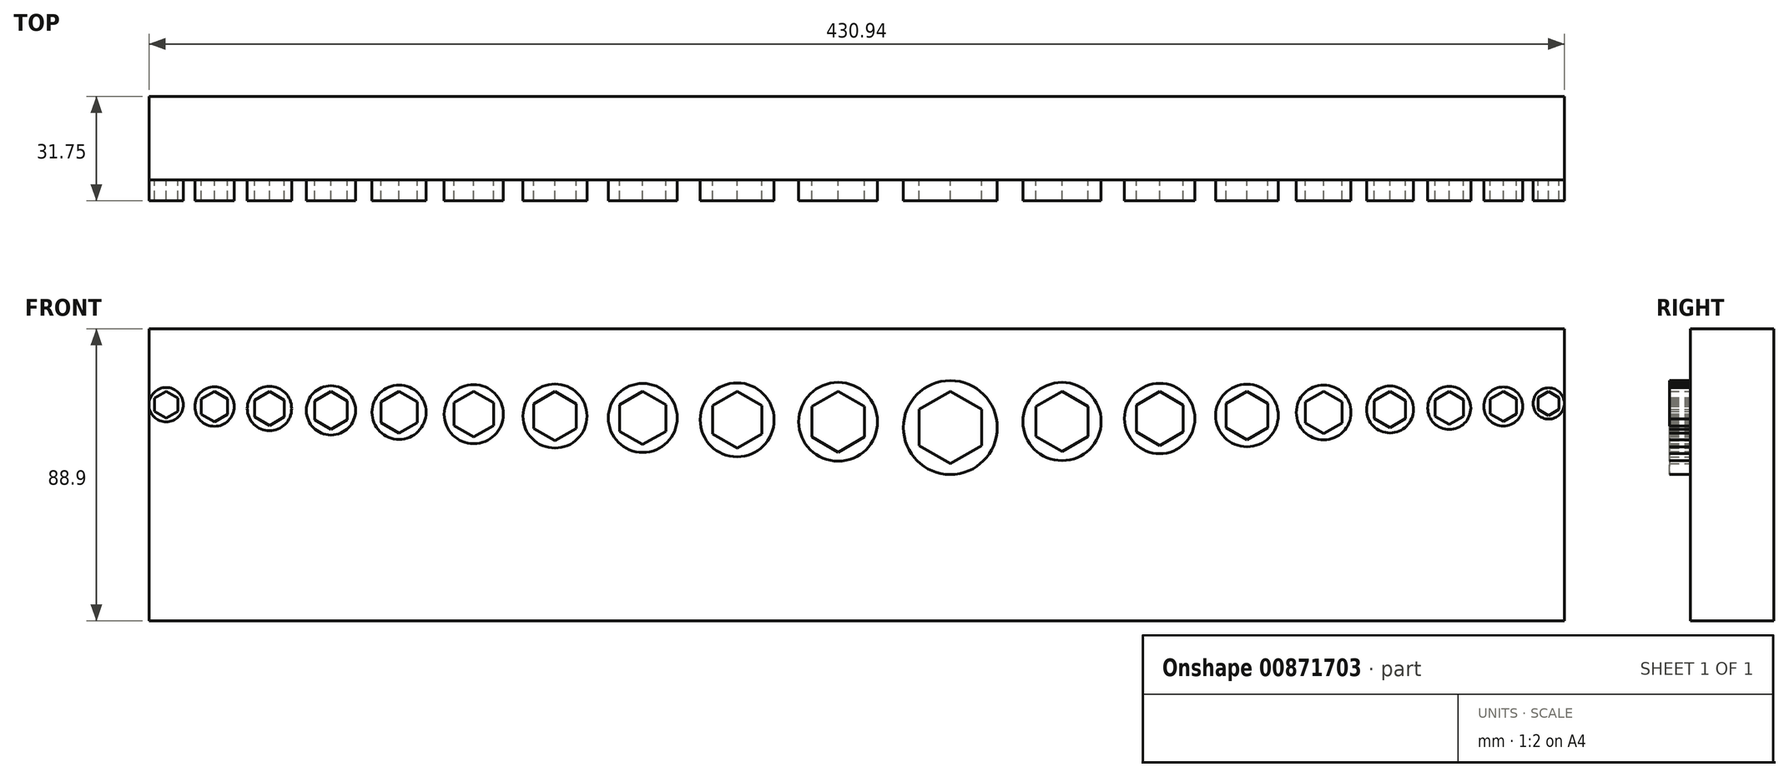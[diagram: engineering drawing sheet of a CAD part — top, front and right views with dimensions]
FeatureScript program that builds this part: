
annotation { "Feature Type Name" : "Feature", "Feature Type Description" : "" }
export const myFeature = defineFeature(function(context is Context, id is Id, definition is map)
    precondition{}
    {
        {
            var Q0;
            Q0=qCreatedBy(makeId("Front.planeOp"),FACE);
            var sketch = newSketch(context, id + "F0", { "sketchPlane" : qUnion([Q0])});
            skPoint(sketch, "E0.middle", {"position": v(0, 0) * mm});
            skLineSegment(sketch, "E1", {"start": v(-190.5, 0) * mm, "end": v(190.5, 0) * mm, "construction": true});
            skSolve(sketch);
        }
        {
            var Q0;
            Q0=qCreatedBy(makeId("Front.planeOp"),FACE);
            var sketch = newSketch(context, id + "F1", { "sketchPlane" : qUnion([Q0])});
            skCircle(sketch, "E2.cCircle", {"center": v(17, -9.24) * mm, "radius": 8 * mm, "construction": true});
            skLineSegment(sketch, "E2.0", {"start": v(25, -4.62) * mm, "end": v(25, -13.86) * mm});
            skLineSegment(sketch, "E2.1", {"start": v(25, -13.86) * mm, "end": v(17, -18.48) * mm});
            skLineSegment(sketch, "E2.2", {"start": v(17, -18.48) * mm, "end": v(9, -13.86) * mm});
            skLineSegment(sketch, "E2.3", {"start": v(9, -13.86) * mm, "end": v(9, -4.62) * mm});
            skLineSegment(sketch, "E2.4", {"start": v(9, -4.62) * mm, "end": v(17, 0) * mm});
            skLineSegment(sketch, "E2.5", {"start": v(17, 0) * mm, "end": v(25, -4.62) * mm});
            skPoint(sketch, "E2.0.midPoint", {"position": v(25, -9.24) * mm});
            skCircle(sketch, "E3", {"center": v(17, -9.24) * mm, "radius": 12 * mm});
            skLineSegment(sketch, "E4", {"start": v(17, -9.24) * mm, "end": v(9, -9.24) * mm, "construction": true});
            skLineSegment(sketch, "E5", {"start": v(13, -9.24) * mm, "end": v(17, -9.24) * mm, "construction": true});
            skLineSegment(sketch, "E6", {"start": v(25, -9.24) * mm, "end": v(29, -9.24) * mm, "construction": true});
            skCircle(sketch, "E7.cCircle", {"center": v(-13.74, -8.66) * mm, "radius": 7.5 * mm, "construction": true});
            skLineSegment(sketch, "E7.0", {"start": v(-6.24, -4.33) * mm, "end": v(-6.24, -13) * mm});
            skLineSegment(sketch, "E7.1", {"start": v(-6.24, -13) * mm, "end": v(-13.74, -17.32) * mm});
            skLineSegment(sketch, "E7.2", {"start": v(-13.74, -17.32) * mm, "end": v(-21.24, -13) * mm});
            skLineSegment(sketch, "E7.3", {"start": v(-21.24, -13) * mm, "end": v(-21.24, -4.33) * mm});
            skLineSegment(sketch, "E7.4", {"start": v(-21.24, -4.33) * mm, "end": v(-13.74, 0) * mm});
            skLineSegment(sketch, "E7.5", {"start": v(-13.74, 0) * mm, "end": v(-6.24, -4.33) * mm});
            skPoint(sketch, "E7.0.midPoint", {"position": v(-6.24, -8.66) * mm});
            skCircle(sketch, "E8", {"center": v(-13.74, -8.66) * mm, "radius": 11.25 * mm});
            skLineSegment(sketch, "E9", {"start": v(-13.74, -8.66) * mm, "end": v(-21.24, -8.66) * mm, "construction": true});
            skLineSegment(sketch, "E10", {"start": v(-17.5, -8.66) * mm, "end": v(-13.74, -8.66) * mm, "construction": true});
            skLineSegment(sketch, "E11", {"start": v(-6.24, -8.66) * mm, "end": v(-2.5, -8.66) * mm, "construction": true});
            skLineSegment(sketch, "E12", {"start": v(-13.74, 0) * mm, "end": v(-13.74, -17.32) * mm, "construction": true});
            skLineSegment(sketch, "E13", {"start": v(17, 0) * mm, "end": v(17, -18.48) * mm, "construction": true});
            skLineSegment(sketch, "E14", {"start": v(-2.5, -8.66) * mm, "end": v(5, -8.66) * mm, "construction": true});
            skCircle(sketch, "E15.cCircle", {"center": v(-42.48, -8.08) * mm, "radius": 7 * mm, "construction": true});
            skLineSegment(sketch, "E15.0", {"start": v(-35.48, -4.04) * mm, "end": v(-35.48, -12.12) * mm});
            skLineSegment(sketch, "E15.1", {"start": v(-35.48, -12.12) * mm, "end": v(-42.48, -16.17) * mm});
            skLineSegment(sketch, "E15.2", {"start": v(-42.48, -16.17) * mm, "end": v(-49.48, -12.12) * mm});
            skLineSegment(sketch, "E15.3", {"start": v(-49.48, -12.12) * mm, "end": v(-49.48, -4.04) * mm});
            skLineSegment(sketch, "E15.4", {"start": v(-49.48, -4.04) * mm, "end": v(-42.48, 0) * mm});
            skLineSegment(sketch, "E15.5", {"start": v(-42.48, 0) * mm, "end": v(-35.48, -4.04) * mm});
            skPoint(sketch, "E15.0.midPoint", {"position": v(-35.48, -8.08) * mm});
            skCircle(sketch, "E16", {"center": v(-42.48, -8.08) * mm, "radius": 10.5 * mm});
            skLineSegment(sketch, "E17", {"start": v(-42.48, -8.08) * mm, "end": v(-49.48, -8.08) * mm, "construction": true});
            skLineSegment(sketch, "E18", {"start": v(-45.98, -8.08) * mm, "end": v(-42.48, -8.08) * mm, "construction": true});
            skLineSegment(sketch, "E19", {"start": v(-35.48, -8.08) * mm, "end": v(-31.98, -8.08) * mm, "construction": true});
            skLineSegment(sketch, "E20", {"start": v(-42.48, 0) * mm, "end": v(-42.48, -16.17) * mm, "construction": true});
            skLineSegment(sketch, "E21", {"start": v(-31.98, -8.08) * mm, "end": v(-24.98, -8.08) * mm, "construction": true});
            skCircle(sketch, "E22.cCircle", {"center": v(-69.21, -7.5) * mm, "radius": 6.5 * mm, "construction": true});
            skLineSegment(sketch, "E22.0", {"start": v(-62.71, -3.75) * mm, "end": v(-62.71, -11.26) * mm});
            skLineSegment(sketch, "E22.1", {"start": v(-62.71, -11.26) * mm, "end": v(-69.21, -15.01) * mm});
            skLineSegment(sketch, "E22.2", {"start": v(-69.21, -15.01) * mm, "end": v(-75.71, -11.26) * mm});
            skLineSegment(sketch, "E22.3", {"start": v(-75.71, -11.26) * mm, "end": v(-75.71, -3.75) * mm});
            skLineSegment(sketch, "E22.4", {"start": v(-75.71, -3.75) * mm, "end": v(-69.21, 0) * mm});
            skLineSegment(sketch, "E22.5", {"start": v(-69.21, 0) * mm, "end": v(-62.71, -3.75) * mm});
            skPoint(sketch, "E22.0.midPoint", {"position": v(-62.71, -7.5) * mm});
            skCircle(sketch, "E23", {"center": v(-69.21, -7.5) * mm, "radius": 9.75 * mm});
            skLineSegment(sketch, "E24", {"start": v(-69.21, -7.5) * mm, "end": v(-75.71, -7.5) * mm, "construction": true});
            skLineSegment(sketch, "E25", {"start": v(-72.46, -7.5) * mm, "end": v(-69.21, -7.5) * mm, "construction": true});
            skLineSegment(sketch, "E26", {"start": v(-62.71, -7.5) * mm, "end": v(-59.46, -7.5) * mm, "construction": true});
            skLineSegment(sketch, "E27", {"start": v(-69.21, 0) * mm, "end": v(-69.21, -15.01) * mm, "construction": true});
            skCircle(sketch, "E28.cCircle", {"center": v(-93.95, -6.93) * mm, "radius": 6 * mm, "construction": true});
            skLineSegment(sketch, "E28.0", {"start": v(-87.95, -3.46) * mm, "end": v(-87.95, -10.4) * mm});
            skLineSegment(sketch, "E28.1", {"start": v(-87.95, -10.4) * mm, "end": v(-93.95, -13.86) * mm});
            skLineSegment(sketch, "E28.2", {"start": v(-93.95, -13.86) * mm, "end": v(-99.95, -10.4) * mm});
            skLineSegment(sketch, "E28.3", {"start": v(-99.95, -10.4) * mm, "end": v(-99.95, -3.46) * mm});
            skLineSegment(sketch, "E28.4", {"start": v(-99.95, -3.46) * mm, "end": v(-93.95, 0) * mm});
            skLineSegment(sketch, "E28.5", {"start": v(-93.95, 0) * mm, "end": v(-87.95, -3.46) * mm});
            skPoint(sketch, "E28.0.midPoint", {"position": v(-87.95, -6.93) * mm});
            skCircle(sketch, "E29", {"center": v(-93.95, -6.93) * mm, "radius": 9 * mm});
            skLineSegment(sketch, "E30", {"start": v(-93.95, -6.93) * mm, "end": v(-99.95, -6.93) * mm, "construction": true});
            skLineSegment(sketch, "E31", {"start": v(-96.95, -6.93) * mm, "end": v(-93.95, -6.93) * mm, "construction": true});
            skLineSegment(sketch, "E32", {"start": v(-87.95, -6.93) * mm, "end": v(-84.95, -6.93) * mm, "construction": true});
            skLineSegment(sketch, "E33", {"start": v(-93.95, 0) * mm, "end": v(-93.95, -13.86) * mm, "construction": true});
            skCircle(sketch, "E34.cCircle", {"center": v(-116.68, -6.35) * mm, "radius": 5.5 * mm, "construction": true});
            skLineSegment(sketch, "E34.0", {"start": v(-111.18, -3.18) * mm, "end": v(-111.18, -9.53) * mm});
            skLineSegment(sketch, "E34.1", {"start": v(-111.18, -9.53) * mm, "end": v(-116.68, -12.7) * mm});
            skLineSegment(sketch, "E34.2", {"start": v(-116.68, -12.7) * mm, "end": v(-122.18, -9.53) * mm});
            skLineSegment(sketch, "E34.3", {"start": v(-122.18, -9.53) * mm, "end": v(-122.18, -3.18) * mm});
            skLineSegment(sketch, "E34.4", {"start": v(-122.18, -3.18) * mm, "end": v(-116.68, 0) * mm});
            skLineSegment(sketch, "E34.5", {"start": v(-116.68, 0) * mm, "end": v(-111.18, -3.18) * mm});
            skPoint(sketch, "E34.0.midPoint", {"position": v(-111.18, -6.35) * mm});
            skCircle(sketch, "E35", {"center": v(-116.68, -6.35) * mm, "radius": 8.25 * mm});
            skLineSegment(sketch, "E36", {"start": v(-116.68, -6.35) * mm, "end": v(-122.18, -6.35) * mm, "construction": true});
            skLineSegment(sketch, "E37", {"start": v(-119.43, -6.35) * mm, "end": v(-116.68, -6.35) * mm, "construction": true});
            skLineSegment(sketch, "E38", {"start": v(-111.18, -6.35) * mm, "end": v(-108.43, -6.35) * mm, "construction": true});
            skLineSegment(sketch, "E39", {"start": v(-116.68, 0) * mm, "end": v(-116.68, -12.7) * mm, "construction": true});
            skCircle(sketch, "E40.cCircle", {"center": v(-137.4, -5.77) * mm, "radius": 5 * mm, "construction": true});
            skLineSegment(sketch, "E40.0", {"start": v(-132.4, -2.89) * mm, "end": v(-132.4, -8.66) * mm});
            skLineSegment(sketch, "E40.1", {"start": v(-132.4, -8.66) * mm, "end": v(-137.4, -11.55) * mm});
            skLineSegment(sketch, "E40.2", {"start": v(-137.4, -11.55) * mm, "end": v(-142.4, -8.66) * mm});
            skLineSegment(sketch, "E40.3", {"start": v(-142.4, -8.66) * mm, "end": v(-142.4, -2.89) * mm});
            skLineSegment(sketch, "E40.4", {"start": v(-142.4, -2.89) * mm, "end": v(-137.4, 0) * mm});
            skLineSegment(sketch, "E40.5", {"start": v(-137.4, 0) * mm, "end": v(-132.4, -2.89) * mm});
            skPoint(sketch, "E40.0.midPoint", {"position": v(-132.4, -5.77) * mm});
            skCircle(sketch, "E41", {"center": v(-137.4, -5.77) * mm, "radius": 7.5 * mm});
            skLineSegment(sketch, "E42", {"start": v(-137.4, -5.77) * mm, "end": v(-142.4, -5.77) * mm, "construction": true});
            skLineSegment(sketch, "E43", {"start": v(-139.9, -5.77) * mm, "end": v(-137.4, -5.77) * mm, "construction": true});
            skLineSegment(sketch, "E44", {"start": v(-132.4, -5.77) * mm, "end": v(-129.9, -5.77) * mm, "construction": true});
            skLineSegment(sketch, "E45", {"start": v(-137.4, 0) * mm, "end": v(-137.4, -11.55) * mm, "construction": true});
            skCircle(sketch, "E46.cCircle", {"center": v(-156.13, -5.2) * mm, "radius": 4.5 * mm, "construction": true});
            skLineSegment(sketch, "E46.0", {"start": v(-151.63, -2.6) * mm, "end": v(-151.63, -7.8) * mm});
            skLineSegment(sketch, "E46.1", {"start": v(-151.63, -7.8) * mm, "end": v(-156.13, -10.4) * mm});
            skLineSegment(sketch, "E46.2", {"start": v(-156.13, -10.4) * mm, "end": v(-160.63, -7.8) * mm});
            skLineSegment(sketch, "E46.3", {"start": v(-160.63, -7.8) * mm, "end": v(-160.63, -2.6) * mm});
            skLineSegment(sketch, "E46.4", {"start": v(-160.63, -2.6) * mm, "end": v(-156.13, 0) * mm});
            skLineSegment(sketch, "E46.5", {"start": v(-156.13, 0) * mm, "end": v(-151.63, -2.6) * mm});
            skPoint(sketch, "E46.0.midPoint", {"position": v(-151.63, -5.2) * mm});
            skCircle(sketch, "E47", {"center": v(-156.13, -5.2) * mm, "radius": 6.75 * mm});
            skLineSegment(sketch, "E48", {"start": v(-156.13, -5.2) * mm, "end": v(-160.63, -5.2) * mm, "construction": true});
            skLineSegment(sketch, "E49", {"start": v(-158.38, -5.2) * mm, "end": v(-156.13, -5.2) * mm, "construction": true});
            skLineSegment(sketch, "E50", {"start": v(-151.63, -5.2) * mm, "end": v(-149.38, -5.2) * mm, "construction": true});
            skLineSegment(sketch, "E51", {"start": v(-156.13, 0) * mm, "end": v(-156.13, -10.4) * mm, "construction": true});
            skCircle(sketch, "E52.cCircle", {"center": v(-172.86, -4.62) * mm, "radius": 4 * mm, "construction": true});
            skLineSegment(sketch, "E52.0", {"start": v(-168.86, -2.3) * mm, "end": v(-168.86, -6.93) * mm});
            skLineSegment(sketch, "E52.1", {"start": v(-168.86, -6.93) * mm, "end": v(-172.86, -9.24) * mm});
            skLineSegment(sketch, "E52.2", {"start": v(-172.86, -9.24) * mm, "end": v(-176.86, -6.93) * mm});
            skLineSegment(sketch, "E52.3", {"start": v(-176.86, -6.93) * mm, "end": v(-176.86, -2.3) * mm});
            skLineSegment(sketch, "E52.4", {"start": v(-176.86, -2.3) * mm, "end": v(-172.86, 0) * mm});
            skLineSegment(sketch, "E52.5", {"start": v(-172.86, 0) * mm, "end": v(-168.86, -2.3) * mm});
            skPoint(sketch, "E52.0.midPoint", {"position": v(-168.86, -4.62) * mm});
            skCircle(sketch, "E53", {"center": v(-172.86, -4.62) * mm, "radius": 6 * mm});
            skLineSegment(sketch, "E54", {"start": v(-172.86, -4.62) * mm, "end": v(-176.86, -4.62) * mm, "construction": true});
            skLineSegment(sketch, "E55", {"start": v(-174.86, -4.62) * mm, "end": v(-172.86, -4.62) * mm, "construction": true});
            skLineSegment(sketch, "E56", {"start": v(-168.86, -4.62) * mm, "end": v(-166.86, -4.62) * mm, "construction": true});
            skLineSegment(sketch, "E57", {"start": v(-172.86, 0) * mm, "end": v(-172.86, -9.24) * mm, "construction": true});
            skLineSegment(sketch, "E58", {"start": v(-166.86, -4.62) * mm, "end": v(-162.86, -4.62) * mm, "construction": true});
            skLineSegment(sketch, "E59", {"start": v(29, -9.24) * mm, "end": v(37, -9.24) * mm, "construction": true});
            skLineSegment(sketch, "E60", {"start": v(-59.46, -7.5) * mm, "end": v(-52.96, -7.5) * mm, "construction": true});
            skLineSegment(sketch, "E61", {"start": v(-84.95, -6.93) * mm, "end": v(-78.95, -6.93) * mm, "construction": true});
            skLineSegment(sketch, "E62", {"start": v(-108.43, -6.35) * mm, "end": v(-102.93, -6.35) * mm, "construction": true});
            skLineSegment(sketch, "E63", {"start": v(-149.38, -5.2) * mm, "end": v(-144.88, -5.2) * mm, "construction": true});
            skLineSegment(sketch, "E64", {"start": v(-129.9, -5.77) * mm, "end": v(-124.9, -5.77) * mm, "construction": true});
            skCircle(sketch, "E65.cCircle", {"center": v(-187.58, -4.04) * mm, "radius": 3.5 * mm, "construction": true});
            skLineSegment(sketch, "E65.0", {"start": v(-184.08, -2.02) * mm, "end": v(-184.08, -6.06) * mm});
            skLineSegment(sketch, "E65.1", {"start": v(-184.08, -6.06) * mm, "end": v(-187.58, -8.08) * mm});
            skLineSegment(sketch, "E65.2", {"start": v(-187.58, -8.08) * mm, "end": v(-191.08, -6.06) * mm});
            skLineSegment(sketch, "E65.3", {"start": v(-191.08, -6.06) * mm, "end": v(-191.08, -2.02) * mm});
            skLineSegment(sketch, "E65.4", {"start": v(-191.08, -2.02) * mm, "end": v(-187.58, 0) * mm});
            skLineSegment(sketch, "E65.5", {"start": v(-187.58, 0) * mm, "end": v(-184.08, -2.02) * mm});
            skPoint(sketch, "E65.0.midPoint", {"position": v(-184.08, -4.04) * mm});
            skCircle(sketch, "E66", {"center": v(-187.58, -4.04) * mm, "radius": 5.25 * mm});
            skLineSegment(sketch, "E67", {"start": v(-187.58, -4.04) * mm, "end": v(-191.08, -4.04) * mm, "construction": true});
            skLineSegment(sketch, "E68", {"start": v(-189.33, -4.04) * mm, "end": v(-187.58, -4.04) * mm, "construction": true});
            skLineSegment(sketch, "E69", {"start": v(-184.08, -4.04) * mm, "end": v(-182.33, -4.04) * mm, "construction": true});
            skLineSegment(sketch, "E70", {"start": v(-187.58, 0) * mm, "end": v(-187.58, -8.08) * mm, "construction": true});
            skLineSegment(sketch, "E71", {"start": v(-182.33, -4.04) * mm, "end": v(-178.83, -4.04) * mm, "construction": true});
            skSolve(sketch);
        }
        {
            var Q0;
            Q0=qCreatedBy(makeId("Front.planeOp"),FACE);
            var sketch = newSketch(context, id + "F2", { "sketchPlane" : qUnion([Q0])});
            skCircle(sketch, "E72.cCircle", {"center": v(51.17, -11) * mm, "radius": 9.53 * mm, "construction": true});
            skLineSegment(sketch, "E72.0", {"start": v(60.7, -5.5) * mm, "end": v(60.7, -16.5) * mm});
            skLineSegment(sketch, "E72.1", {"start": v(60.7, -16.5) * mm, "end": v(51.17, -22) * mm});
            skLineSegment(sketch, "E72.2", {"start": v(51.17, -22) * mm, "end": v(41.65, -16.5) * mm});
            skLineSegment(sketch, "E72.3", {"start": v(41.65, -16.5) * mm, "end": v(41.65, -5.5) * mm});
            skLineSegment(sketch, "E72.4", {"start": v(41.65, -5.5) * mm, "end": v(51.17, 0) * mm});
            skLineSegment(sketch, "E72.5", {"start": v(51.17, 0) * mm, "end": v(60.7, -5.5) * mm});
            skPoint(sketch, "E72.0.midPoint", {"position": v(60.7, -11) * mm});
            skCircle(sketch, "E73", {"center": v(51.17, -11) * mm, "radius": 14.29 * mm});
            skLineSegment(sketch, "E74", {"start": v(51.17, -11) * mm, "end": v(41.65, -11) * mm, "construction": true});
            skLineSegment(sketch, "E75", {"start": v(46.4, -11) * mm, "end": v(51.17, -11) * mm, "construction": true});
            skLineSegment(sketch, "E76", {"start": v(60.7, -11) * mm, "end": v(65.46, -11) * mm, "construction": true});
            skLineSegment(sketch, "E77", {"start": v(51.17, 0) * mm, "end": v(51.17, -22) * mm, "construction": true});
            skPoint(sketch, "E78.0", {"position": v(37, -9.24) * mm});
            skCircle(sketch, "E79.cCircle", {"center": v(85.18, -9.17) * mm, "radius": 7.94 * mm, "construction": true});
            skLineSegment(sketch, "E79.0", {"start": v(93.12, -4.58) * mm, "end": v(93.12, -13.75) * mm});
            skLineSegment(sketch, "E79.1", {"start": v(93.12, -13.75) * mm, "end": v(85.18, -18.33) * mm});
            skLineSegment(sketch, "E79.2", {"start": v(85.18, -18.33) * mm, "end": v(77.25, -13.75) * mm});
            skLineSegment(sketch, "E79.3", {"start": v(77.25, -13.75) * mm, "end": v(77.25, -4.58) * mm});
            skLineSegment(sketch, "E79.4", {"start": v(77.25, -4.58) * mm, "end": v(85.18, 0) * mm});
            skLineSegment(sketch, "E79.5", {"start": v(85.18, 0) * mm, "end": v(93.12, -4.58) * mm});
            skPoint(sketch, "E79.0.midPoint", {"position": v(93.12, -9.17) * mm});
            skCircle(sketch, "E80", {"center": v(85.18, -9.17) * mm, "radius": 11.9 * mm});
            skLineSegment(sketch, "E81", {"start": v(85.18, -9.17) * mm, "end": v(77.25, -9.17) * mm, "construction": true});
            skLineSegment(sketch, "E82", {"start": v(81.22, -9.17) * mm, "end": v(85.18, -9.17) * mm, "construction": true});
            skLineSegment(sketch, "E83", {"start": v(93.12, -9.17) * mm, "end": v(97.1, -9.17) * mm, "construction": true});
            skLineSegment(sketch, "E84", {"start": v(85.18, 0) * mm, "end": v(85.18, -18.33) * mm, "construction": true});
            skLineSegment(sketch, "E85", {"start": v(73.28, -9.17) * mm, "end": v(65.34, -9.17) * mm, "construction": true});
            skCircle(sketch, "E86.cCircle", {"center": v(114.91, -8.25) * mm, "radius": 7.14 * mm, "construction": true});
            skLineSegment(sketch, "E86.0", {"start": v(122.06, -4.12) * mm, "end": v(122.06, -12.37) * mm});
            skLineSegment(sketch, "E86.1", {"start": v(122.06, -12.37) * mm, "end": v(114.91, -16.5) * mm});
            skLineSegment(sketch, "E86.2", {"start": v(114.91, -16.5) * mm, "end": v(107.77, -12.37) * mm});
            skLineSegment(sketch, "E86.3", {"start": v(107.77, -12.37) * mm, "end": v(107.77, -4.12) * mm});
            skLineSegment(sketch, "E86.4", {"start": v(107.77, -4.12) * mm, "end": v(114.91, 0) * mm});
            skLineSegment(sketch, "E86.5", {"start": v(114.91, 0) * mm, "end": v(122.06, -4.12) * mm});
            skPoint(sketch, "E86.0.midPoint", {"position": v(122.06, -8.25) * mm});
            skCircle(sketch, "E87", {"center": v(114.91, -8.25) * mm, "radius": 10.72 * mm});
            skLineSegment(sketch, "E88", {"start": v(114.91, -8.25) * mm, "end": v(107.77, -8.25) * mm, "construction": true});
            skLineSegment(sketch, "E89", {"start": v(111.34, -8.25) * mm, "end": v(114.91, -8.25) * mm, "construction": true});
            skLineSegment(sketch, "E90", {"start": v(122.06, -8.25) * mm, "end": v(125.63, -8.25) * mm, "construction": true});
            skLineSegment(sketch, "E91", {"start": v(114.91, 0) * mm, "end": v(114.91, -16.5) * mm, "construction": true});
            skLineSegment(sketch, "E92", {"start": v(104.2, -8.25) * mm, "end": v(97.06, -8.25) * mm, "construction": true});
            skCircle(sketch, "E93.cCircle", {"center": v(141.47, -7.33) * mm, "radius": 6.35 * mm, "construction": true});
            skLineSegment(sketch, "E93.0", {"start": v(147.82, -3.67) * mm, "end": v(147.82, -11) * mm});
            skLineSegment(sketch, "E93.1", {"start": v(147.82, -11) * mm, "end": v(141.47, -14.66) * mm});
            skLineSegment(sketch, "E93.2", {"start": v(141.47, -14.66) * mm, "end": v(135.12, -11) * mm});
            skLineSegment(sketch, "E93.3", {"start": v(135.12, -11) * mm, "end": v(135.12, -3.67) * mm});
            skLineSegment(sketch, "E93.4", {"start": v(135.12, -3.67) * mm, "end": v(141.47, 0) * mm});
            skLineSegment(sketch, "E93.5", {"start": v(141.47, 0) * mm, "end": v(147.82, -3.67) * mm});
            skPoint(sketch, "E93.0.midPoint", {"position": v(147.82, -7.33) * mm});
            skCircle(sketch, "E94", {"center": v(141.47, -7.33) * mm, "radius": 9.53 * mm});
            skLineSegment(sketch, "E95", {"start": v(141.47, -7.33) * mm, "end": v(135.12, -7.33) * mm, "construction": true});
            skLineSegment(sketch, "E96", {"start": v(138.3, -7.33) * mm, "end": v(141.47, -7.33) * mm, "construction": true});
            skLineSegment(sketch, "E97", {"start": v(147.82, -7.33) * mm, "end": v(151, -7.33) * mm, "construction": true});
            skLineSegment(sketch, "E98", {"start": v(141.47, 0) * mm, "end": v(141.47, -14.66) * mm, "construction": true});
            skLineSegment(sketch, "E99", {"start": v(131.94, -7.33) * mm, "end": v(125.6, -7.33) * mm, "construction": true});
            skCircle(sketch, "E100.cCircle", {"center": v(164.84, -6.42) * mm, "radius": 5.56 * mm, "construction": true});
            skLineSegment(sketch, "E100.0", {"start": v(170.4, -3.2) * mm, "end": v(170.4, -9.62) * mm});
            skLineSegment(sketch, "E100.1", {"start": v(170.4, -9.62) * mm, "end": v(164.84, -12.83) * mm});
            skLineSegment(sketch, "E100.2", {"start": v(164.84, -12.83) * mm, "end": v(159.28, -9.62) * mm});
            skLineSegment(sketch, "E100.3", {"start": v(159.28, -9.62) * mm, "end": v(159.28, -3.2) * mm});
            skLineSegment(sketch, "E100.4", {"start": v(159.28, -3.2) * mm, "end": v(164.84, 0) * mm});
            skLineSegment(sketch, "E100.5", {"start": v(164.84, 0) * mm, "end": v(170.4, -3.2) * mm});
            skPoint(sketch, "E100.0.midPoint", {"position": v(170.4, -6.42) * mm});
            skCircle(sketch, "E101", {"center": v(164.84, -6.42) * mm, "radius": 8.33 * mm});
            skLineSegment(sketch, "E102", {"start": v(164.84, -6.42) * mm, "end": v(159.28, -6.42) * mm, "construction": true});
            skLineSegment(sketch, "E103", {"start": v(162.06, -6.42) * mm, "end": v(164.84, -6.42) * mm, "construction": true});
            skLineSegment(sketch, "E104", {"start": v(170.4, -6.42) * mm, "end": v(173.17, -6.42) * mm, "construction": true});
            skLineSegment(sketch, "E105", {"start": v(164.84, 0) * mm, "end": v(164.84, -12.83) * mm, "construction": true});
            skLineSegment(sketch, "E106", {"start": v(156.5, -6.42) * mm, "end": v(150.95, -6.42) * mm, "construction": true});
            skCircle(sketch, "E107.cCircle", {"center": v(185.03, -5.5) * mm, "radius": 4.76 * mm, "construction": true});
            skLineSegment(sketch, "E107.0", {"start": v(189.8, -2.75) * mm, "end": v(189.8, -8.25) * mm});
            skLineSegment(sketch, "E107.1", {"start": v(189.8, -8.25) * mm, "end": v(185.03, -11) * mm});
            skLineSegment(sketch, "E107.2", {"start": v(185.03, -11) * mm, "end": v(180.27, -8.25) * mm});
            skLineSegment(sketch, "E107.3", {"start": v(180.27, -8.25) * mm, "end": v(180.27, -2.75) * mm});
            skLineSegment(sketch, "E107.4", {"start": v(180.27, -2.75) * mm, "end": v(185.03, 0) * mm});
            skLineSegment(sketch, "E107.5", {"start": v(185.03, 0) * mm, "end": v(189.8, -2.75) * mm});
            skPoint(sketch, "E107.0.midPoint", {"position": v(189.8, -5.5) * mm});
            skCircle(sketch, "E108", {"center": v(185.03, -5.5) * mm, "radius": 7.14 * mm});
            skLineSegment(sketch, "E109", {"start": v(185.03, -5.5) * mm, "end": v(180.27, -5.5) * mm, "construction": true});
            skLineSegment(sketch, "E110", {"start": v(182.65, -5.5) * mm, "end": v(185.03, -5.5) * mm, "construction": true});
            skLineSegment(sketch, "E111", {"start": v(189.8, -5.5) * mm, "end": v(192.17, -5.5) * mm, "construction": true});
            skLineSegment(sketch, "E112", {"start": v(185.03, 0) * mm, "end": v(185.03, -11) * mm, "construction": true});
            skCircle(sketch, "E113.cCircle", {"center": v(203.07, -5.04) * mm, "radius": 4.37 * mm, "construction": true});
            skLineSegment(sketch, "E113.0", {"start": v(207.44, -2.52) * mm, "end": v(207.44, -7.56) * mm});
            skLineSegment(sketch, "E113.1", {"start": v(207.44, -7.56) * mm, "end": v(203.07, -10.08) * mm});
            skLineSegment(sketch, "E113.2", {"start": v(203.07, -10.08) * mm, "end": v(198.7, -7.56) * mm});
            skLineSegment(sketch, "E113.3", {"start": v(198.7, -7.56) * mm, "end": v(198.7, -2.52) * mm});
            skLineSegment(sketch, "E113.4", {"start": v(198.7, -2.52) * mm, "end": v(203.07, 0) * mm});
            skLineSegment(sketch, "E113.5", {"start": v(203.07, 0) * mm, "end": v(207.44, -2.52) * mm});
            skPoint(sketch, "E113.0.midPoint", {"position": v(207.44, -5.04) * mm});
            skCircle(sketch, "E114", {"center": v(203.07, -5.04) * mm, "radius": 6.55 * mm});
            skLineSegment(sketch, "E115", {"start": v(203.07, -5.04) * mm, "end": v(198.7, -5.04) * mm, "construction": true});
            skLineSegment(sketch, "E116", {"start": v(200.89, -5.04) * mm, "end": v(203.07, -5.04) * mm, "construction": true});
            skLineSegment(sketch, "E117", {"start": v(207.44, -5.04) * mm, "end": v(209.62, -5.04) * mm, "construction": true});
            skLineSegment(sketch, "E118", {"start": v(203.07, 0) * mm, "end": v(203.07, -10.08) * mm, "construction": true});
            skCircle(sketch, "E119.cCircle", {"center": v(219.53, -4.58) * mm, "radius": 3.97 * mm, "construction": true});
            skLineSegment(sketch, "E119.0", {"start": v(223.5, -2.3) * mm, "end": v(223.5, -6.87) * mm});
            skLineSegment(sketch, "E119.1", {"start": v(223.5, -6.87) * mm, "end": v(219.53, -9.17) * mm});
            skLineSegment(sketch, "E119.2", {"start": v(219.53, -9.17) * mm, "end": v(215.56, -6.87) * mm});
            skLineSegment(sketch, "E119.3", {"start": v(215.56, -6.87) * mm, "end": v(215.56, -2.3) * mm});
            skLineSegment(sketch, "E119.4", {"start": v(215.56, -2.3) * mm, "end": v(219.53, 0) * mm});
            skLineSegment(sketch, "E119.5", {"start": v(219.53, 0) * mm, "end": v(223.5, -2.3) * mm});
            skPoint(sketch, "E119.0.midPoint", {"position": v(223.5, -4.58) * mm});
            skCircle(sketch, "E120", {"center": v(219.53, -4.58) * mm, "radius": 5.95 * mm});
            skLineSegment(sketch, "E121", {"start": v(219.53, -4.58) * mm, "end": v(215.56, -4.58) * mm, "construction": true});
            skLineSegment(sketch, "E122", {"start": v(217.54, -4.58) * mm, "end": v(219.53, -4.58) * mm, "construction": true});
            skLineSegment(sketch, "E123", {"start": v(223.5, -4.58) * mm, "end": v(225.48, -4.58) * mm, "construction": true});
            skLineSegment(sketch, "E124", {"start": v(219.53, 0) * mm, "end": v(219.53, -9.17) * mm, "construction": true});
            skCircle(sketch, "E125.cCircle", {"center": v(233.34, -3.67) * mm, "radius": 3.18 * mm, "construction": true});
            skLineSegment(sketch, "E125.0", {"start": v(236.52, -1.83) * mm, "end": v(236.52, -5.5) * mm});
            skLineSegment(sketch, "E125.1", {"start": v(236.52, -5.5) * mm, "end": v(233.34, -7.33) * mm});
            skLineSegment(sketch, "E125.2", {"start": v(233.34, -7.33) * mm, "end": v(230.17, -5.5) * mm});
            skLineSegment(sketch, "E125.3", {"start": v(230.17, -5.5) * mm, "end": v(230.17, -1.83) * mm});
            skLineSegment(sketch, "E125.4", {"start": v(230.17, -1.83) * mm, "end": v(233.34, 0) * mm});
            skLineSegment(sketch, "E125.5", {"start": v(233.34, 0) * mm, "end": v(236.52, -1.83) * mm});
            skPoint(sketch, "E125.0.midPoint", {"position": v(236.52, -3.67) * mm});
            skCircle(sketch, "E126", {"center": v(233.34, -3.67) * mm, "radius": 4.76 * mm});
            skLineSegment(sketch, "E127", {"start": v(233.34, -3.67) * mm, "end": v(230.17, -3.67) * mm, "construction": true});
            skLineSegment(sketch, "E128", {"start": v(231.76, -3.67) * mm, "end": v(233.34, -3.67) * mm, "construction": true});
            skLineSegment(sketch, "E129", {"start": v(236.52, -3.67) * mm, "end": v(238.1, -3.67) * mm, "construction": true});
            skLineSegment(sketch, "E130", {"start": v(233.34, 0) * mm, "end": v(233.34, -7.33) * mm, "construction": true});
            skLineSegment(sketch, "E131", {"start": v(177.88, -5.5) * mm, "end": v(173.12, -5.5) * mm, "construction": true});
            skLineSegment(sketch, "E132", {"start": v(196.52, -5.04) * mm, "end": v(192.16, -5.04) * mm, "construction": true});
            skLineSegment(sketch, "E133", {"start": v(213.57, -4.58) * mm, "end": v(209.6, -4.58) * mm, "construction": true});
            skLineSegment(sketch, "E134", {"start": v(228.58, -3.67) * mm, "end": v(225.4, -3.67) * mm, "construction": true});
            skSolve(sketch);
        }
        {
            var Q0;
            Q0=qCreatedBy(makeId("Front.planeOp"),FACE);
            var sketch = newSketch(context, id + "F3", { "sketchPlane" : qUnion([Q0])});
            skLineSegment(sketch, "E135.bottom", {"start": v(238.1, 19.05) * mm, "end": v(-192.83, 19.05) * mm});
            skLineSegment(sketch, "E135.top", {"start": v(238.1, -69.85) * mm, "end": v(-192.83, -69.85) * mm});
            skLineSegment(sketch, "E135.left", {"start": v(238.1, 19.05) * mm, "end": v(238.1, -69.85) * mm});
            skLineSegment(sketch, "E135.right", {"start": v(-192.83, 19.05) * mm, "end": v(-192.83, -69.85) * mm});
            skPoint(sketch, "E135.middle", {"position": v(22.64, -25.4) * mm});
            skCircle(sketch, "E136.0", {"center": v(233.34, -3.67) * mm, "radius": 4.76 * mm, "construction": true});
            skLineSegment(sketch, "E137.0", {"start": v(-190.5, 0) * mm, "end": v(190.5, 0) * mm, "construction": true});
            skCircle(sketch, "E138.0", {"center": v(-187.58, -4.04) * mm, "radius": 5.25 * mm});
            skSolve(sketch);
        }
        {
            var Q0;
            Q0 = qSketchRegion(id + "F3", true);
            extrude(context, id + "F4", {"entities" : qUnion([Q0]), "oppositeDirection" : true, "depth" : 25.4 * mm, "offsetDistance" : 25.4 * mm});
        }
        {
            var Q0;
            Q0 = qSketchRegion(id + "F1", true);
            extrude(context, id + "F5", {"entities" : qUnion([Q0]), "operationType" : NewBodyOperationType.ADD, "depth" : 6.35 * mm, "offsetDistance" : 25.4 * mm});
        }
        {
            var Q0;
            Q0 = qSketchRegion(id + "F2", true);
            var Q1;
            Q1=makeQuery(id+"F5.opExtrude","CAP_FACE",FACE,{"disambiguationData":[OSD([sQuery(id+"F1.wireOp",EDGE,"E2.0"),sQuery(id+"F1.wireOp",EDGE,"E2.1"),sQuery(id+"F1.wireOp",EDGE,"E2.2"),sQuery(id+"F1.wireOp",EDGE,"E2.3"),sQuery(id+"F1.wireOp",EDGE,"E2.4"),sQuery(id+"F1.wireOp",EDGE,"E2.5"),sQuery(id+"F1.wireOp",EDGE,"E3")])],"isStart":false});
            extrude(context, id + "F6", {"entities" : qUnion([Q0]), "operationType" : NewBodyOperationType.ADD, "endBound" : BoundingType.UP_TO_SURFACE, "depth" : 6.35 * mm, "endBoundEntityFace" : qUnion([Q1]), "offsetDistance" : 25.4 * mm});
        }
    });
